# Revit family: GNW_A3-Arched-(2)
name_source: partatom
category: Windows
revit_build: Autodesk Revit 2016 (Build: 20150220_1215(x64)
units: mm (PartAtom-declared; Revit-internal decimal feet)

## family parameters
Always vertical = Yes
Cut with Voids When Loaded = No
Host = Wall
Room Calculation Point = No
Shared = No

## types (1)
- Arched Window
    Cavity Closer Depth = 85 mm  [stored 0.278871 ft]
    Cavity Closer Offset from Ext = 102.5 mm  [stored 0.336286 ft]
    Cavity Closer Width = 50 mm  [stored 0.164042 ft]
    Cill Depth = 87.5 mm  [stored 0.287073 ft]
    Default Head Height = 2110 mm  [stored 6.92257 ft]
    Frame Depth = 68 mm
    FrameOffset - External = 50 mm  [stored 0.164042 ft]
    Glazing Thickness = 24 mm  [stored 0.0787402 ft]
    Height = 1350 mm  [stored 4.42913 ft]
    Keynote = L10
    Manufacturer = Revit
    Material Frame = Window Frame
    Material Glass = Glass
    Material Trim = Window Frame
    Operation = UserDefined
    Rough Height = 1350 mm  [stored 4.42913 ft]
    Rough Width = 900 mm  [stored 2.95276 ft]
    Vis - Cavity Closers = Yes
    Wall Closure = By host
    Width = 900 mm  [stored 2.95276 ft]
    Window Board Extension = 25 mm  [stored 0.082021 ft]
    Window Board Projection = 25 mm  [stored 0.082021 ft]
    Wrap Layers (Ext) from Ext = 102.5 mm  [stored 0.336286 ft]
    Wrap Layers (Int) from Ext = 177.5 mm

note: [stored X ft] marks values corroborated as IEEE doubles in the binary element streams (Revit-internal decimal feet)

## geometry (parser evidence)
native form markers: Sweep x1
no freeform markers — native parametric forms only
